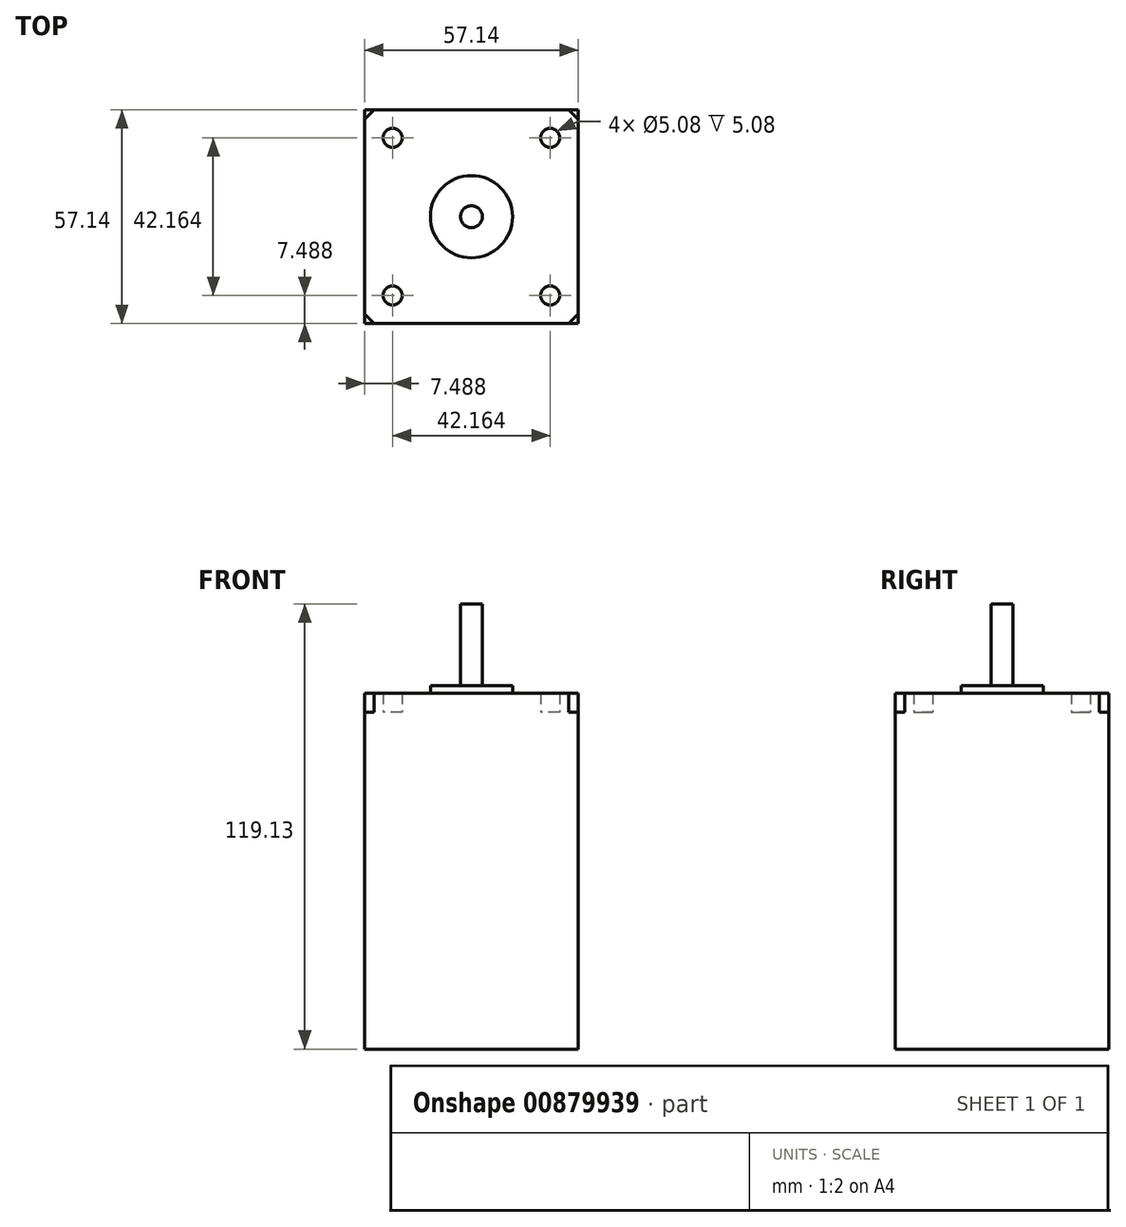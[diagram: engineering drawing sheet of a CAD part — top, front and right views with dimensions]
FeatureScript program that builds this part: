
annotation { "Feature Type Name" : "Feature", "Feature Type Description" : "" }
export const myFeature = defineFeature(function(context is Context, id is Id, definition is map)
    precondition{}
    {
        {
            var Q0;
            Q0=qCreatedBy(makeId("Top.planeOp"),FACE);
            var sketch = newSketch(context, id + "F0", { "sketchPlane" : qUnion([Q0])});
            skLineSegment(sketch, "E0.bottom", {"start": v(-28.57, 28.58) * mm, "end": v(28.58, 28.58) * mm});
            skLineSegment(sketch, "E0.top", {"start": v(-28.58, -28.58) * mm, "end": v(28.58, -28.58) * mm});
            skLineSegment(sketch, "E0.left", {"start": v(-28.57, 28.58) * mm, "end": v(-28.58, -28.58) * mm});
            skLineSegment(sketch, "E0.right", {"start": v(28.58, 28.57) * mm, "end": v(28.58, -28.58) * mm});
            skPoint(sketch, "E0.middle", {"position": v(0, 0) * mm});
            skCircle(sketch, "E1.MirrorC", {"center": v(21.08, 21.08) * mm, "radius": 2.54 * mm});
            skCircle(sketch, "E2.MirrorC", {"center": v(-21.08, 21.08) * mm, "radius": 2.54 * mm});
            skCircle(sketch, "E3.MirrorC", {"center": v(-21.08, -21.08) * mm, "radius": 2.54 * mm});
            skCircle(sketch, "E4.MirrorC", {"center": v(21.08, -21.08) * mm, "radius": 2.54 * mm});
            skSolve(sketch);
        }
        {
            var Q0;
            Q0 = qSketchRegion(id + "F0", true);
            extrude(context, id + "F1", {"entities" : qUnion([Q0]), "depth" : 5.08 * mm, "offsetDistance" : 25.4 * mm});
        }
        {
            var Q0;
            Q0=makeQuery(id+"F1.opExtrude","SWEPT_EDGE",EDGE,{"disambiguationData":[OSD([sQuery(id+"F0.wireOp",EDGE,"E0.bottom"),sQuery(id+"F0.wireOp",EDGE,"E0.left")])]});
            var Q1;
            Q1=makeQuery(id+"F1.opExtrude","SWEPT_EDGE",EDGE,{"disambiguationData":[OSD([sQuery(id+"F0.wireOp",EDGE,"E0.bottom"),sQuery(id+"F0.wireOp",EDGE,"E0.right")])]});
            var Q2;
            Q2=makeQuery(id+"F1.opExtrude","SWEPT_EDGE",EDGE,{"disambiguationData":[OSD([sQuery(id+"F0.wireOp",EDGE,"E0.top"),sQuery(id+"F0.wireOp",EDGE,"E0.right")])]});
            var Q3;
            Q3=makeQuery(id+"F1.opExtrude","SWEPT_EDGE",EDGE,{"disambiguationData":[OSD([sQuery(id+"F0.wireOp",EDGE,"E0.top"),sQuery(id+"F0.wireOp",EDGE,"E0.left")])]});
            chamfer(context, id + "F2", {"entities" : qUnion([Q0, Q1, Q2, Q3]), "width" : 2.54 * mm, "tangentPropagation" : true});
        }
        {
            var Q0;
            Q0=makeQuery(id+"F1.opExtrude","CAP_FACE",FACE,{"disambiguationData":[OSD([sQuery(id+"F0.wireOp",EDGE,"E0.bottom"),sQuery(id+"F0.wireOp",EDGE,"E0.top"),sQuery(id+"F0.wireOp",EDGE,"E0.left"),sQuery(id+"F0.wireOp",EDGE,"E0.right"),sQuery(id+"F0.wireOp",EDGE,"fyZ1z60k-7AHA-eRB5-oKYR-1XDmCmRi3dKU"),sQuery(id+"F0.wireOp",EDGE,"E1.MirrorC"),sQuery(id+"F0.wireOp",EDGE,"a798e0bc-6e89-46cb-91b8-99804b8acdd50.MirrorC"),sQuery(id+"F0.wireOp",EDGE,"a798e0bc-6e89-46cb-91b8-99804b8acdd51.MirrorC")])],"isStart":true});
            var sketch = newSketch(context, id + "F3", { "sketchPlane" : qUnion([Q0])});
            skLineSegment(sketch, "E5.bottom", {"start": v(28.58, -28.58) * mm, "end": v(-28.58, -28.58) * mm});
            skLineSegment(sketch, "E5.top", {"start": v(28.58, 28.58) * mm, "end": v(-28.58, 28.58) * mm});
            skLineSegment(sketch, "E5.left", {"start": v(28.58, -28.58) * mm, "end": v(28.58, 28.58) * mm});
            skLineSegment(sketch, "E5.right", {"start": v(-28.58, -28.58) * mm, "end": v(-28.58, 28.58) * mm});
            skPoint(sketch, "E5.middle", {"position": v(0, 0) * mm});
            skSolve(sketch);
        }
        {
            var Q0;
            Q0 = qSketchRegion(id + "F3", true);
            extrude(context, id + "F4", {"entities" : qUnion([Q0]), "operationType" : NewBodyOperationType.ADD, "depth" : 90.17 * mm, "offsetDistance" : 25.4 * mm});
        }
        {
            var Q0;
            Q0=makeQuery(id+"F1.opExtrude","CAP_FACE",FACE,{"disambiguationData":[OSD([sQuery(id+"F0.wireOp",EDGE,"E0.bottom"),sQuery(id+"F0.wireOp",EDGE,"E0.top"),sQuery(id+"F0.wireOp",EDGE,"E0.left"),sQuery(id+"F0.wireOp",EDGE,"E0.right"),sQuery(id+"F0.wireOp",EDGE,"fyZ1z60k-7AHA-eRB5-oKYR-1XDmCmRi3dKU"),sQuery(id+"F0.wireOp",EDGE,"E1.MirrorC"),sQuery(id+"F0.wireOp",EDGE,"a798e0bc-6e89-46cb-91b8-99804b8acdd50.MirrorC"),sQuery(id+"F0.wireOp",EDGE,"a798e0bc-6e89-46cb-91b8-99804b8acdd51.MirrorC")])],"isStart":false});
            var sketch = newSketch(context, id + "F5", { "sketchPlane" : qUnion([Q0])});
            skCircle(sketch, "E6", {"center": v(0, 0) * mm, "radius": 10.99 * mm});
            skSolve(sketch);
        }
        {
            var Q0;
            Q0=makeQuery(id+"F5.imprint","IMPRINT",FACE,{"disambiguationData":[TD([[makeQuery(id+"F5.imprint","IMPRINT",EDGE,{"derivedFrom":sQuery(id+"F5.wireOp",EDGE,"E6")}),1.0]])]});
            var Q1;
            Q1=sQuery(id+"F5.wireOp",EDGE,"E6");
            extrude(context, id + "F6", {"entities" : qUnion([Q0]), "operationType" : NewBodyOperationType.ADD, "surfaceEntities" : qUnion([Q1]), "depth" : 2.03 * mm, "offsetDistance" : 25.4 * mm});
        }
        {
            var Q0;
            Q0=makeQuery(id+"F6.opExtrude","CAP_FACE",FACE,{"disambiguationData":[OSD([sQuery(id+"F5.wireOp",EDGE,"E6")])],"isStart":false});
            var sketch = newSketch(context, id + "F7", { "sketchPlane" : qUnion([Q0])});
            skCircle(sketch, "E7", {"center": v(0, 0) * mm, "radius": 2.92 * mm});
            skSolve(sketch);
        }
        {
            var Q0;
            Q0=makeQuery(id+"F7.imprint","IMPRINT",FACE,{"disambiguationData":[TD([[makeQuery(id+"F7.imprint","IMPRINT",EDGE,{"derivedFrom":sQuery(id+"F7.wireOp",EDGE,"E7")}),1.0]])]});
            var Q1;
            Q1=sQuery(id+"F7.wireOp",EDGE,"E7");
            extrude(context, id + "F8", {"entities" : qUnion([Q0]), "operationType" : NewBodyOperationType.ADD, "surfaceEntities" : qUnion([Q1]), "depth" : 21.84 * mm, "offsetDistance" : 25.4 * mm});
        }
    });
